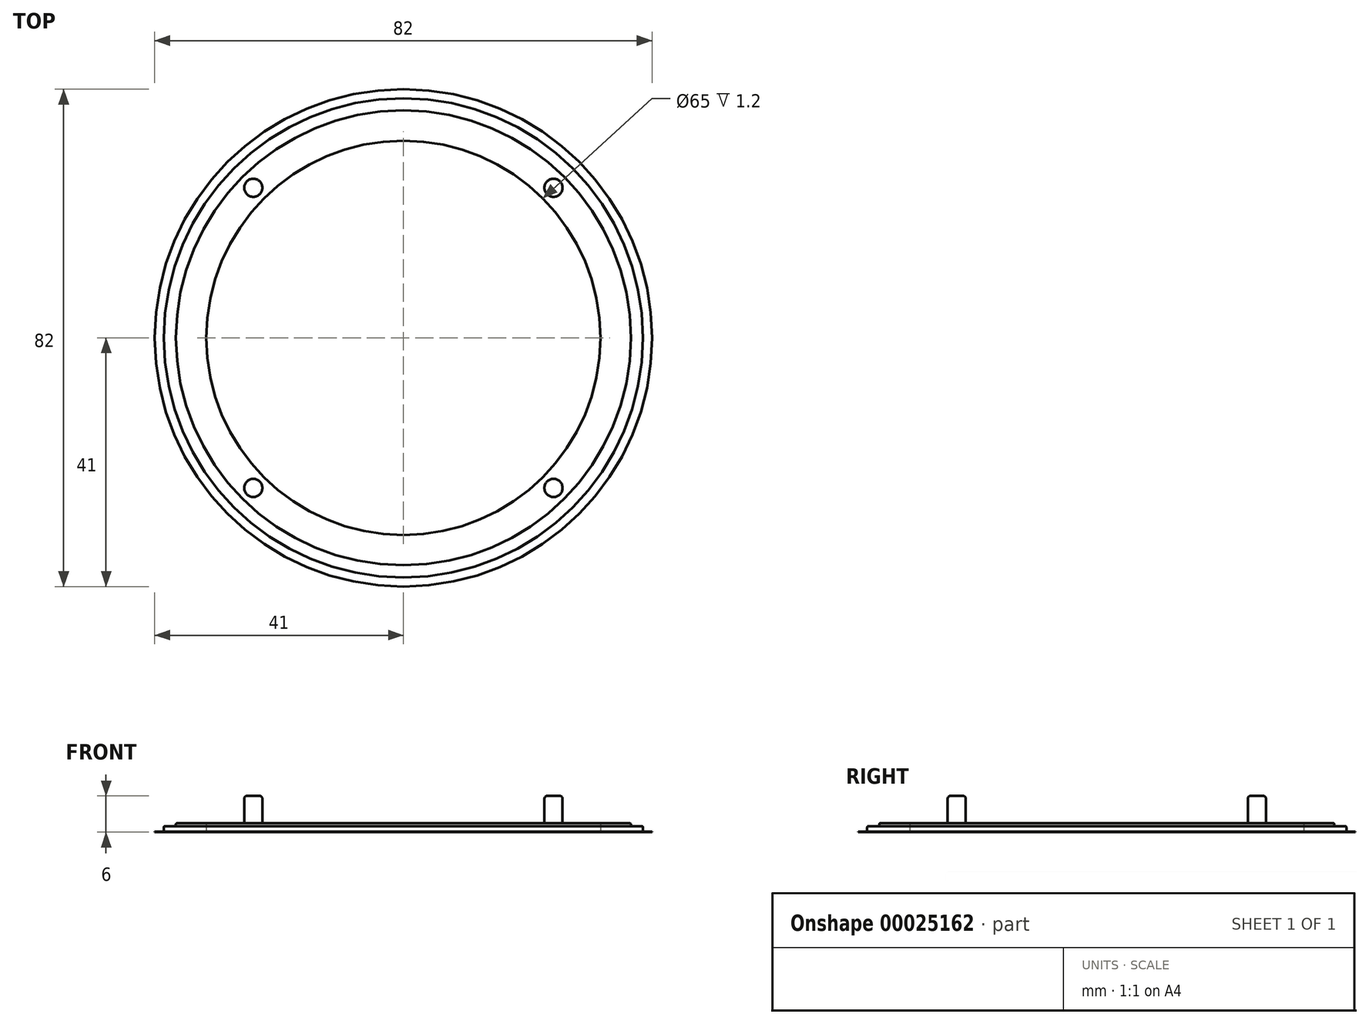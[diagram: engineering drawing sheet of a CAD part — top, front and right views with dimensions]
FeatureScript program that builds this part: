
annotation { "Feature Type Name" : "Feature", "Feature Type Description" : "" }
export const myFeature = defineFeature(function(context is Context, id is Id, definition is map)
    precondition{}
    {
        {
            var Q0;
            Q0=qCreatedBy(makeId("Top.planeOp"),FACE);
            var sketch = newSketch(context, id + "F0", { "sketchPlane" : qUnion([Q0])});
            skCircle(sketch, "E0", {"center": v(0, 0) * mm, "radius": 41 * mm});
            skCircle(sketch, "E1", {"center": v(0, 0) * mm, "radius": 39.5 * mm});
            skCircle(sketch, "E2", {"center": v(0, 0) * mm, "radius": 37.5 * mm});
            skCircle(sketch, "E3", {"center": v(0, 0) * mm, "radius": 32.5 * mm});
            skCircle(sketch, "E4", {"center": v(-24.75, 24.75) * mm, "radius": 1.5 * mm});
            skCircle(sketch, "E5", {"center": v(24.75, 24.75) * mm, "radius": 1.5 * mm});
            skCircle(sketch, "E6", {"center": v(-24.75, -24.75) * mm, "radius": 1.5 * mm});
            skCircle(sketch, "E7", {"center": v(24.75, -24.75) * mm, "radius": 1.5 * mm});
            skCircle(sketch, "E8", {"center": v(0, 0) * mm, "radius": 35 * mm, "construction": true});
            skLineSegment(sketch, "E9.rect.bottom", {"start": v(-24.75, 24.75) * mm, "end": v(24.75, 24.75) * mm, "construction": true});
            skLineSegment(sketch, "E9.rect.top", {"start": v(-24.75, -24.75) * mm, "end": v(24.75, -24.75) * mm, "construction": true});
            skLineSegment(sketch, "E9.rect.left", {"start": v(-24.75, 24.75) * mm, "end": v(-24.75, -24.75) * mm, "construction": true});
            skLineSegment(sketch, "E9.rect.right", {"start": v(24.75, 24.75) * mm, "end": v(24.75, -24.75) * mm, "construction": true});
            skLineSegment(sketch, "E10", {"start": v(0, 0) * mm, "end": v(0, 41) * mm, "construction": true});
            skLineSegment(sketch, "E11", {"start": v(-24.47, 41) * mm, "end": v(24.47, 41) * mm, "construction": true});
            skSolve(sketch);
        }
        {
            var Q0;
            Q0=makeQuery(id+"F0.imprint","IMPRINT",FACE,{"disambiguationData":[TD([[makeQuery(id+"F0.imprint","IMPRINT",EDGE,{"derivedFrom":sQuery(id+"F0.wireOp",EDGE,"E2")}),1.0]])]});
            extrude(context, id + "F1", {"entities" : qUnion([Q0]), "depth" : 1.5 * mm});
        }
        {
            var Q0;
            Q0=makeQuery(id+"F0.imprint","IMPRINT",FACE,{"disambiguationData":[TD([[makeQuery(id+"F0.imprint","IMPRINT",EDGE,{"derivedFrom":sQuery(id+"F0.wireOp",EDGE,"E1")}),1.0]])]});
            extrude(context, id + "F2", {"entities" : qUnion([Q0]), "operationType" : NewBodyOperationType.ADD, "depth" : 1 * mm});
        }
        {
            var Q0;
            Q0=makeQuery(id+"F0.imprint","IMPRINT",FACE,{"disambiguationData":[TD([[makeQuery(id+"F0.imprint","IMPRINT",EDGE,{"derivedFrom":sQuery(id+"F0.wireOp",EDGE,"E0")}),1.0]])]});
            extrude(context, id + "F3", {"entities" : qUnion([Q0]), "operationType" : NewBodyOperationType.ADD, "depth" : .1 * mm});
        }
        {
            var Q0;
            Q0=makeQuery(id+"F0.imprint","IMPRINT",FACE,{"disambiguationData":[TD([[makeQuery(id+"F0.imprint","IMPRINT",EDGE,{"derivedFrom":sQuery(id+"F0.wireOp",EDGE,"E4")}),1.0]])]});
            var Q1;
            Q1=makeQuery(id+"F0.imprint","IMPRINT",FACE,{"disambiguationData":[TD([[makeQuery(id+"F0.imprint","IMPRINT",EDGE,{"derivedFrom":sQuery(id+"F0.wireOp",EDGE,"E5")}),1.0]])]});
            var Q2;
            Q2=makeQuery(id+"F0.imprint","IMPRINT",FACE,{"disambiguationData":[TD([[makeQuery(id+"F0.imprint","IMPRINT",EDGE,{"derivedFrom":sQuery(id+"F0.wireOp",EDGE,"E7")}),1.0]])]});
            var Q3;
            Q3=makeQuery(id+"F0.imprint","IMPRINT",FACE,{"disambiguationData":[TD([[makeQuery(id+"F0.imprint","IMPRINT",EDGE,{"derivedFrom":sQuery(id+"F0.wireOp",EDGE,"E6")}),1.0]])]});
            extrude(context, id + "F4", {"entities" : qUnion([Q0, Q1, Q2, Q3]), "operationType" : NewBodyOperationType.ADD, "depth" : 6 * mm});
        }
        {
            var Q0;
            Q0=makeQuery(id+"F4.opExtrude","CAP_EDGE",EDGE,{"disambiguationData":[OSD([sQuery(id+"F0.wireOp",EDGE,"E4")])],"isStart":false});
            var Q1;
            Q1=makeQuery(id+"F4.opExtrude","CAP_EDGE",EDGE,{"disambiguationData":[OSD([sQuery(id+"F0.wireOp",EDGE,"E6")])],"isStart":false});
            var Q2;
            Q2=makeQuery(id+"F4.opExtrude","CAP_EDGE",EDGE,{"disambiguationData":[OSD([sQuery(id+"F0.wireOp",EDGE,"E7")])],"isStart":false});
            var Q3;
            Q3=makeQuery(id+"F4.opExtrude","CAP_EDGE",EDGE,{"disambiguationData":[OSD([sQuery(id+"F0.wireOp",EDGE,"E5")])],"isStart":false});
            fillet(context, id + "F5", {"entities" : qUnion([Q0, Q1, Q2, Q3]), "radius" : .5 * mm, "tangentPropagation" : true, "allowEdgeOverflow" : false});
        }
        {
            var Q0;
            Q0=makeQuery(id+"F0.imprint","IMPRINT",FACE,{"disambiguationData":[TD([[makeQuery(id+"F0.imprint","IMPRINT",EDGE,{"derivedFrom":sQuery(id+"F0.wireOp",EDGE,"E3")}),1.0]])]});
            extrude(context, id + "F6", {"entities" : qUnion([Q0]), "operationType" : NewBodyOperationType.ADD, "depth" : .1 * mm});
        }
        {
            var Q0;
            Q0=makeQuery(id+"F2.opExtrude","CAP_EDGE",EDGE,{"disambiguationData":[OSD([sQuery(id+"F0.wireOp",EDGE,"E1")])],"isStart":false});
            var Q1;
            Q1=makeQuery(id+"F1.opExtrude","CAP_EDGE",EDGE,{"disambiguationData":[OSD([sQuery(id+"F0.wireOp",EDGE,"E2")])],"isStart":false});
            var Q2;
            Q2=makeQuery(id+"F1.opExtrude","CAP_EDGE",EDGE,{"disambiguationData":[OSD([sQuery(id+"F0.wireOp",EDGE,"E3")])],"isStart":false});
            fillet(context, id + "F7", {"entities" : qUnion([Q0, Q1, Q2]), "radius" : .2 * mm, "tangentPropagation" : true, "allowEdgeOverflow" : false});
        }
        {
            var Q0;
            Q0=qCreatedBy(makeId("Top.planeOp"),FACE);
            cPlane(context, id + "F8", {"entities" : qUnion([Q0]), "cplaneType" : CPlaneType.OFFSET, "offset" : 5 * mm, "width" : 150 * mm, "height" : 150 * mm});
        }
        {
            var Q0;
            Q0=sQuery(id+"F0.wireOp",EDGE,"E11");
            cPlane(context, id + "F9", {"entities" : qUnion([Q0]), "cplaneType" : CPlaneType.LINE_ANGLE, "offset" : 150 * mm, "angle" : 150 * degree, "width" : 150 * mm, "height" : 150 * mm});
        }
    });
